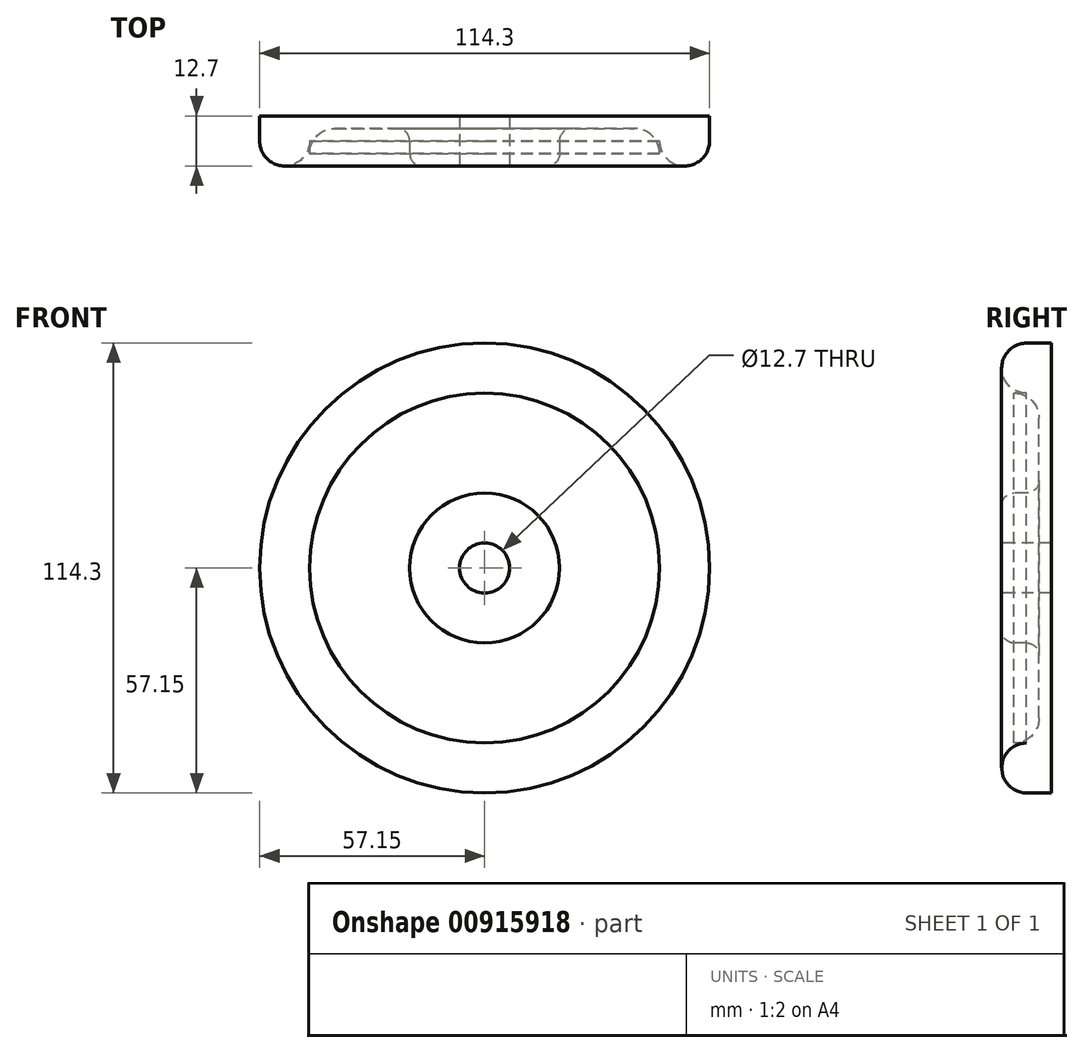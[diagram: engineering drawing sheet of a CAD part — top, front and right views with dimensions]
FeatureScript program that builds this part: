
annotation { "Feature Type Name" : "Feature", "Feature Type Description" : "" }
export const myFeature = defineFeature(function(context is Context, id is Id, definition is map)
    precondition{}
    {
        {
            var Q0;
            Q0=qCreatedBy(makeId("Right.planeOp"),FACE);
            var sketch = newSketch(context, id + "F0", { "sketchPlane" : qUnion([Q0])});
            skLineSegment(sketch, "E0", {"start": v(0, 6.35) * mm, "end": v(0, 57.15) * mm});
            skLineSegment(sketch, "E1", {"start": v(0, 57.15) * mm, "end": v(-6.35, 57.15) * mm});
            skLineSegment(sketch, "E2", {"start": v(-9.52, 44.45) * mm, "end": v(-6.35, 44.45) * mm});
            skLineSegment(sketch, "E3", {"start": v(-3.17, 38.1) * mm, "end": v(-3.17, 19.05) * mm});
            skLineSegment(sketch, "E4", {"start": v(-3.17, 19.05) * mm, "end": v(-12.7, 19.05) * mm});
            skLineSegment(sketch, "E5", {"start": v(-12.7, 19.05) * mm, "end": v(-12.7, 6.35) * mm});
            skLineSegment(sketch, "E6", {"start": v(-12.7, 6.35) * mm, "end": v(0, 6.35) * mm});
            skArc(sketch, "E7", {"start": v(-6.35, 57.15) * mm, "mid": v(-12.7, 50.8) * mm, "end": v(-6.35, 44.45) * mm});
            skPoint(sketch, "E8.visualSharp", {"position": v(-3.17, 44.45) * mm});
            skArc(sketch, "E8.filletArc", {"start": v(-3.17, 38.1) * mm, "mid": v(-5.03, 42.6) * mm, "end": v(-9.52, 44.45) * mm});
            skLineSegment(sketch, "E9", {"start": v(0, 0) * mm, "end": v(21.41, 0) * mm, "construction": true});
            skSolve(sketch);
        }
        {
            var Q0;
            Q0 = qSketchRegion(id + "F0", true);
            var Q1;
            Q1=sQuery(id+"F0.wireOp",EDGE,"E9");
            revolve(context, id + "F1", {"surfaceOperationType" : NewSurfaceOperationType.NEW, "entities" : qUnion([Q0]), "axis" : qUnion([Q1]), "revolveType" : RevolveType.FULL});
        }
        {
            var Q0;
            Q0=makeQuery(id+"F1.opRevolve","SWEPT_EDGE",EDGE,{"disambiguationData":[OSD([sQuery(id+"F0.wireOp",EDGE,"E3"),sQuery(id+"F0.wireOp",EDGE,"E4")])]});
            var Q1;
            Q1=makeQuery(id+"F1.opRevolve","SWEPT_EDGE",EDGE,{"disambiguationData":[OSD([sQuery(id+"F0.wireOp",EDGE,"E4"),sQuery(id+"F0.wireOp",EDGE,"E5")])]});
            fillet(context, id + "F2", {"entities" : qUnion([Q0, Q1]), "radius" : 3.17 * mm, "tangentPropagation" : true, "allowEdgeOverflow" : false});
        }
    });
